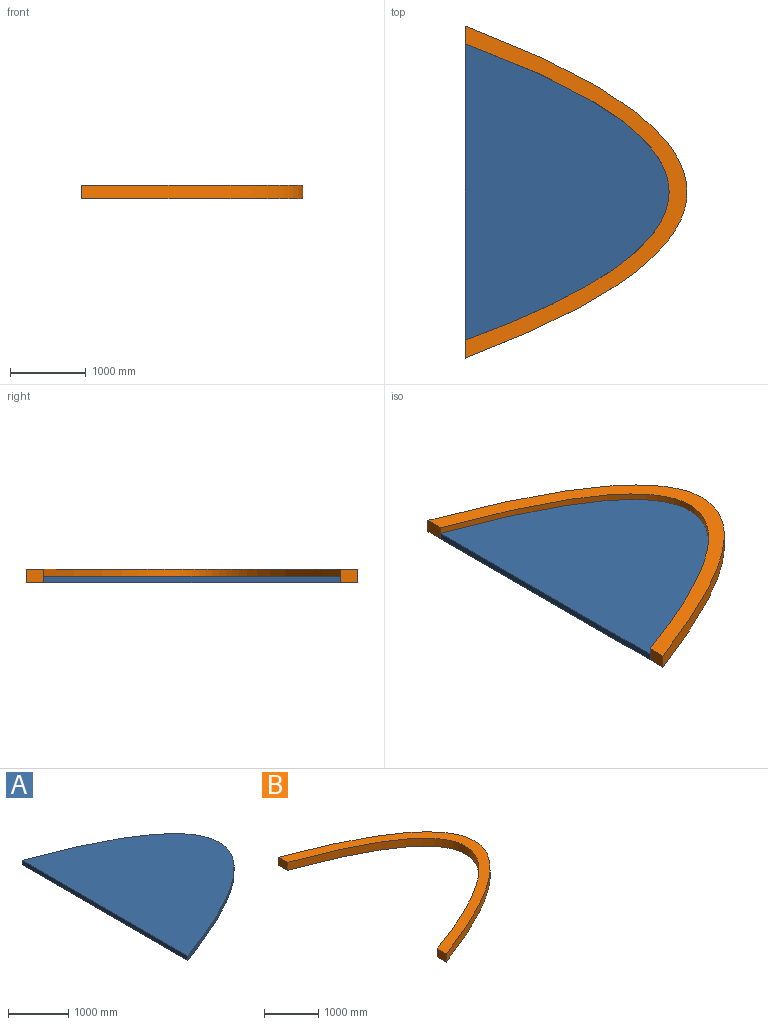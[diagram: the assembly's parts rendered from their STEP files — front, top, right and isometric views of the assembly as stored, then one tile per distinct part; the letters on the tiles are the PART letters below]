
ASSEMBLY  parts=2 mates=1
PART A: 4 faces, bbox 3693.3x3898.9x88.9 mm
  f0: extruded ~3898.9x2686.05mm, area 617369.5mm2, adj f1,f2,f3
  f1: plane 3898.9x88.9mm, normal (-1,0,0), area 346612.2mm2, adj f0,f2,f3
  f2: plane 3898.9x3693.32mm, normal (0,0,1), area 6981760.2mm2, adj f0,f1
  f3: plane 3898.9x3693.32mm, normal (0,0,-1), area 6981760.2mm2, adj f0,f1
PART B: 6 faces, bbox 4016.4x4368.8x177.8 mm
  f0: plane 234.95x177.8mm, normal (-1,0,0), area 41774.1mm2, adj f1,f3,f4,f5
  f1: extruded ~3898.9x2686.05mm, area 1234739mm2, adj f0,f2,f4,f5
  f2: plane 234.95x177.8mm, normal (-1,0,0), area 41774.1mm2, adj f1,f3,f4,f5
  f3: extruded ~4368.8x2921mm, area 1357294mm2, adj f0,f2,f4,f5
  f4: plane 4368.8x4016.38mm, normal (0,0,1), area 1525749.6mm2, adj f0,f1,f2,f3
  f5: plane 4368.8x4016.38mm, normal (0,0,-1), area 1525749.6mm2, adj f0,f1,f2,f3
PLACE A t=(9300.3,-2184.4,0)mm
PLACE B t=(9300.3,-2184.4,0)mm
MATE fastened B.f5 <-> A.f3  axis (0,0,-1) through (-1074.44,-1949.45,0)mm
